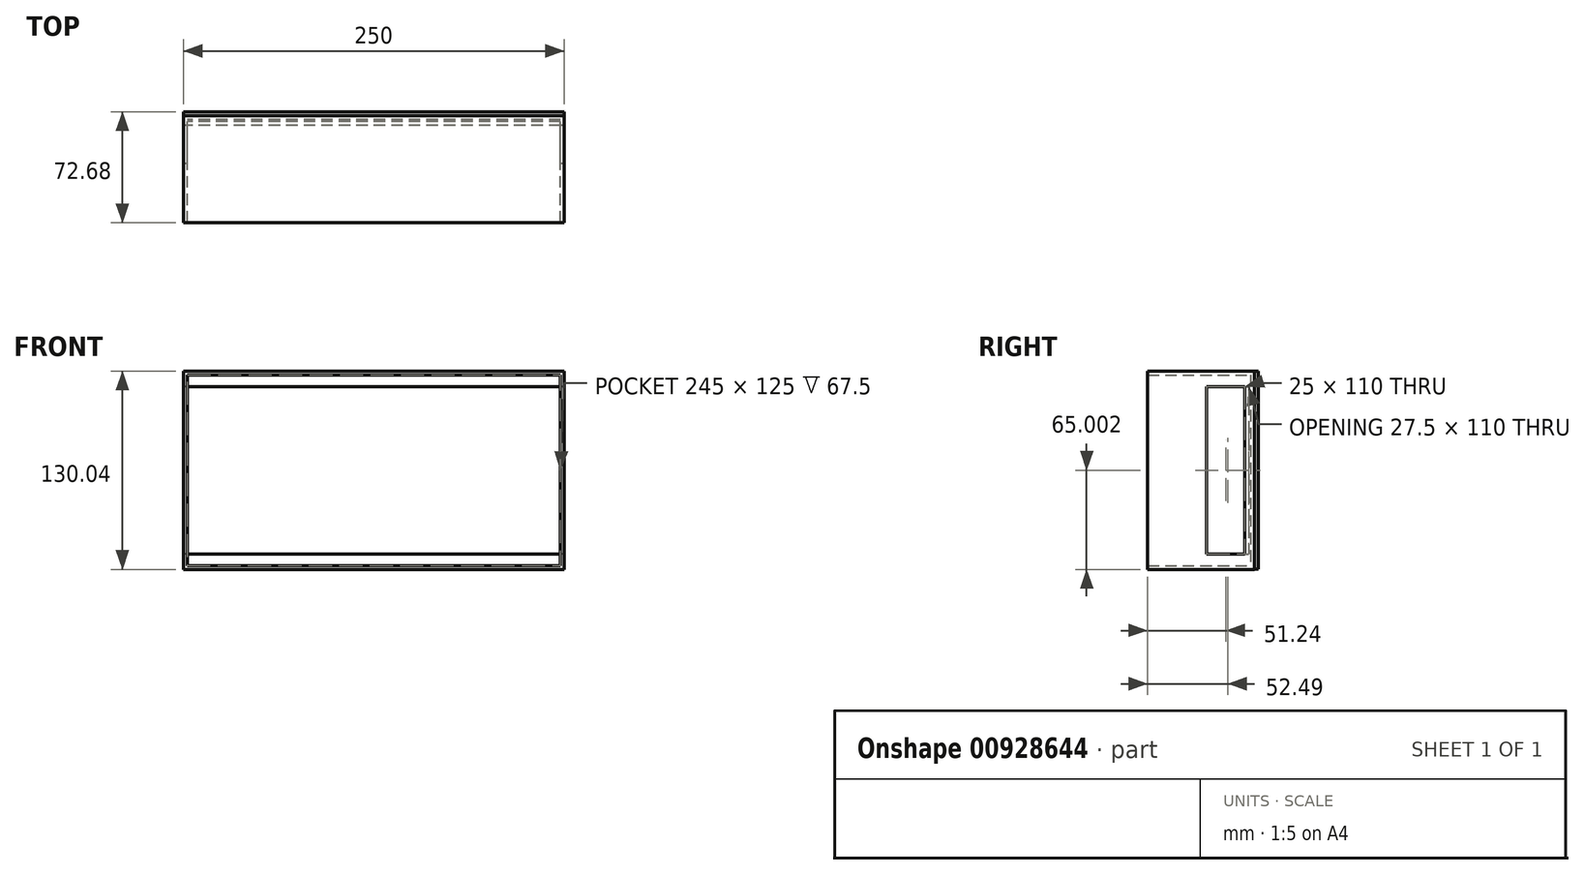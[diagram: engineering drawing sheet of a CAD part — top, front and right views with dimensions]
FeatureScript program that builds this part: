
annotation { "Feature Type Name" : "Feature", "Feature Type Description" : "" }
export const myFeature = defineFeature(function(context is Context, id is Id, definition is map)
    precondition{}
    {
        {
            var Q0;
            Q0=qCreatedBy(makeId("Front.planeOp"),FACE);
            var sketch = newSketch(context, id + "F0", { "sketchPlane" : qUnion([Q0])});
            skLineSegment(sketch, "E0.bottom", {"start": v(-125, 73.3) * mm, "end": v(125, 73.3) * mm});
            skLineSegment(sketch, "E0.top", {"start": v(-125, -56.7) * mm, "end": v(125, -56.7) * mm});
            skLineSegment(sketch, "E0.left", {"start": v(-125, 73.3) * mm, "end": v(-125, -56.7) * mm});
            skLineSegment(sketch, "E0.right", {"start": v(125, 73.3) * mm, "end": v(125, -56.7) * mm});
            skSolve(sketch);
        }
        {
            var Q0;
            Q0=makeQuery(id+"F0.imprint","IMPRINT",FACE,{"disambiguationData":[TD([[makeQuery(id+"F0.imprint","IMPRINT",EDGE,{"derivedFrom":sQuery(id+"F0.wireOp",EDGE,"E0.bottom")}),-1.0]])]});
            extrude(context, id + "F1", {"entities" : qUnion([Q0]), "depth" : 2.5 * mm, "offsetDistance" : 25 * mm});
        }
        {
            var Q0;
            Q0=qCreatedBy(makeId("Right.planeOp"),FACE);
            var sketch = newSketch(context, id + "F2", { "sketchPlane" : qUnion([Q0])});
            skLineSegment(sketch, "E1.bottom", {"start": v(-72.68, 73.27) * mm, "end": v(-2.68, 73.27) * mm});
            skLineSegment(sketch, "E1.top", {"start": v(-72.68, -56.73) * mm, "end": v(-2.68, -56.73) * mm});
            skLineSegment(sketch, "E1.left", {"start": v(-72.68, 73.27) * mm, "end": v(-72.68, -56.73) * mm});
            skLineSegment(sketch, "E1.right", {"start": v(-2.68, 73.27) * mm, "end": v(-2.68, -56.73) * mm});
            skLineSegment(sketch, "E2.bottom", {"start": v(-33.94, 63.27) * mm, "end": v(-8.94, 63.27) * mm});
            skLineSegment(sketch, "E2.top", {"start": v(-33.94, -46.73) * mm, "end": v(-8.94, -46.73) * mm});
            skLineSegment(sketch, "E2.left", {"start": v(-33.94, 63.27) * mm, "end": v(-33.94, -46.73) * mm});
            skLineSegment(sketch, "E2.right", {"start": v(-8.94, 63.27) * mm, "end": v(-8.94, -46.73) * mm});
            skSolve(sketch);
        }
        {
            var Q0;
            Q0=makeQuery(id+"F2.imprint","IMPRINT",FACE,{"disambiguationData":[TD([[makeQuery(id+"F2.imprint","IMPRINT",EDGE,{"derivedFrom":sQuery(id+"F2.wireOp",EDGE,"E1.bottom")}),-1.0]])]});
            extrude(context, id + "F3", {"entities" : qUnion([Q0]), "endBound" : BoundingType.SYMMETRIC, "depth" : 250 * mm, "offsetDistance" : 25 * mm});
        }
        {
            var Q0;
            Q0=makeQuery(id+"F3.opExtrude","SWEPT_FACE",FACE,{"disambiguationData":[OSD([sQuery(id+"F2.wireOp",EDGE,"E1.left")])]});
            var Q1;
            Q1=makeQuery(id+"F3.opExtrude","SWEPT_FACE",FACE,{"disambiguationData":[OSD([sQuery(id+"F2.wireOp",EDGE,"E2.left")])]});
            var Q2;
            Q2=makeQuery(id+"F3.opExtrude","SWEPT_FACE",FACE,{"disambiguationData":[OSD([sQuery(id+"F2.wireOp",EDGE,"E2.top")])]});
            var Q3;
            Q3=makeQuery(id+"F3.opExtrude","SWEPT_FACE",FACE,{"disambiguationData":[OSD([sQuery(id+"F2.wireOp",EDGE,"E2.bottom")])]});
            shell(context, id + "F4", {"entities" : qUnion([Q0, Q1, Q2, Q3]), "thickness" : 2.5 * mm});
        }
    });
